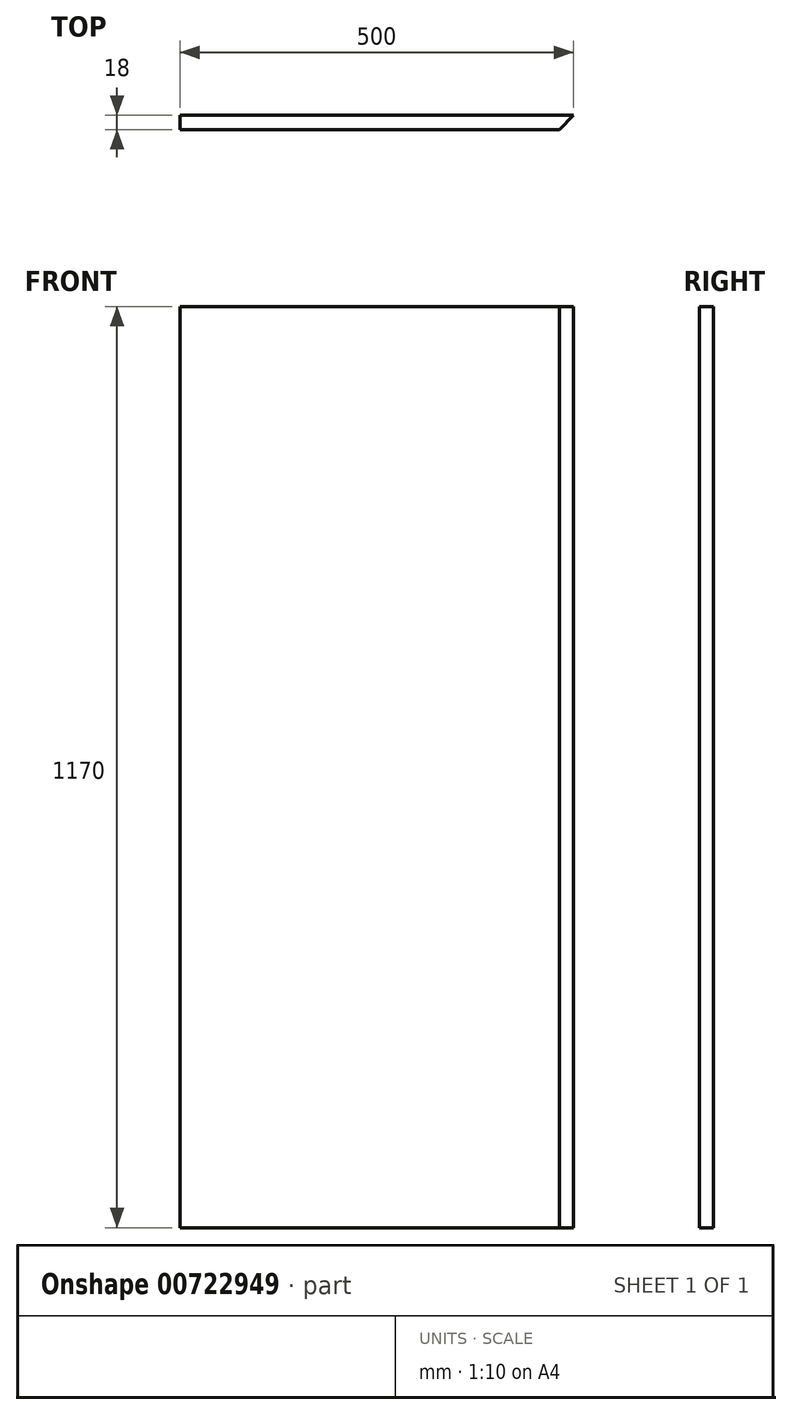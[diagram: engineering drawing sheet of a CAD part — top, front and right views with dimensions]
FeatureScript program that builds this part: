
annotation { "Feature Type Name" : "Feature", "Feature Type Description" : "" }
export const myFeature = defineFeature(function(context is Context, id is Id, definition is map)
    precondition{}
    {
        {
            var Q0;
            Q0=qCreatedBy(makeId("Front.planeOp"),FACE);
            var sketch = newSketch(context, id + "F0", { "sketchPlane" : qUnion([Q0])});
            skLineSegment(sketch, "E0.bottom", {"start": v(-250, 585) * mm, "end": v(250, 585) * mm});
            skLineSegment(sketch, "E0.top", {"start": v(-250, -585) * mm, "end": v(250, -585) * mm});
            skLineSegment(sketch, "E0.left", {"start": v(-250, 585) * mm, "end": v(-250, -585) * mm});
            skLineSegment(sketch, "E0.right", {"start": v(250, 585) * mm, "end": v(250, -585) * mm});
            skLineSegment(sketch, "E1", {"start": v(-250, 585) * mm, "end": v(250, -585) * mm, "construction": true});
            skLineSegment(sketch, "E2", {"start": v(250, 585) * mm, "end": v(-250, -585) * mm, "construction": true});
            skSolve(sketch);
        }
        {
            var Q0;
            Q0 = qSketchRegion(id + "F0", true);
            extrude(context, id + "F1", {"entities" : qUnion([Q0]), "depth" : 18 * mm, "offsetDistance" : 25 * mm});
        }
        {
            var Q0;
            Q0=makeQuery(id+"F1.opExtrude","CAP_EDGE",EDGE,{"disambiguationData":[OSD([sQuery(id+"F0.wireOp",EDGE,"E0.right")])],"isStart":false});
            chamfer(context, id + "F2", {"entities" : qUnion([Q0]), "width" : 18 * mm, "tangentPropagation" : true});
        }
    });
